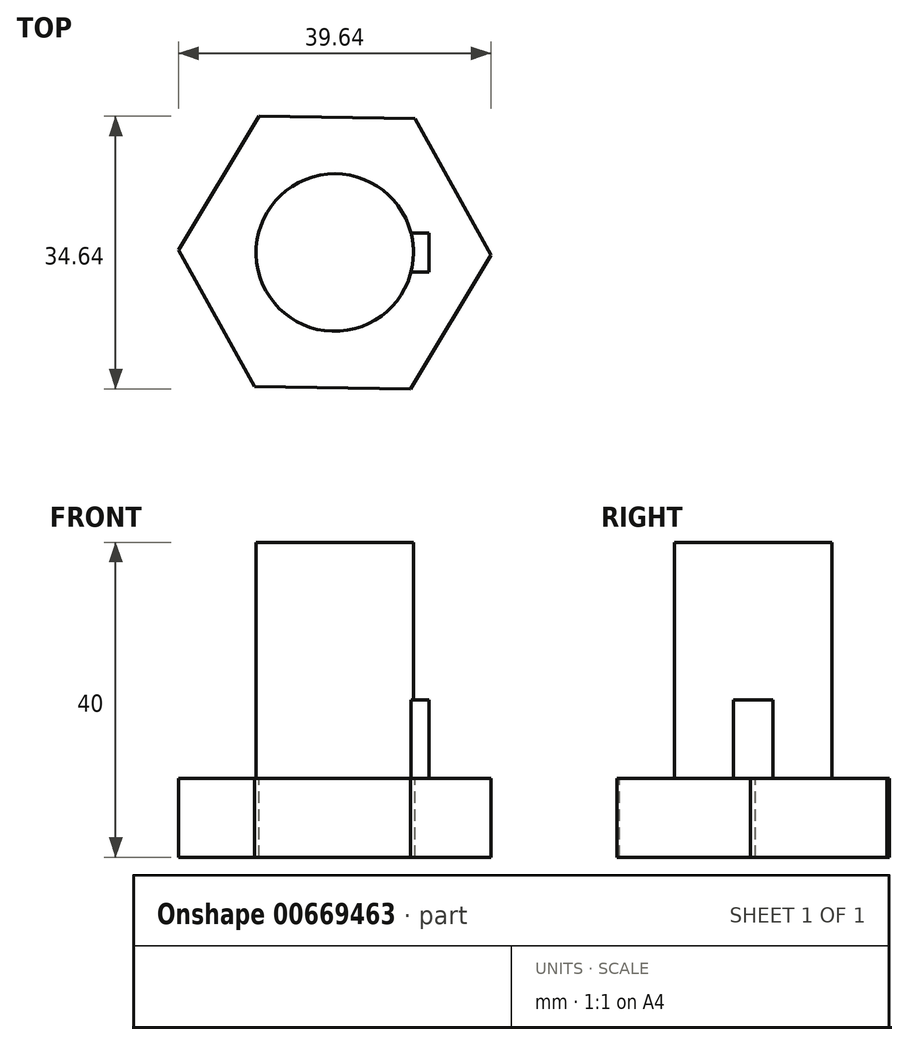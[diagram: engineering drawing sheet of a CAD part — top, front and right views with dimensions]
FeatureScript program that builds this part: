
annotation { "Feature Type Name" : "Feature", "Feature Type Description" : "" }
export const myFeature = defineFeature(function(context is Context, id is Id, definition is map)
    precondition{}
    {
        {
            var Q0;
            Q0=qCreatedBy(makeId("Top.planeOp"),FACE);
            var sketch = newSketch(context, id + "F0", { "sketchPlane" : qUnion([Q0])});
            skCircle(sketch, "E0", {"center": v(0, 0) * mm, "radius": 10 * mm});
            skLineSegment(sketch, "E1.bottom", {"start": v(9.68, 2.5) * mm, "end": v(12, 2.5) * mm});
            skLineSegment(sketch, "E1.top", {"start": v(9.68, -2.5) * mm, "end": v(12, -2.5) * mm});
            skLineSegment(sketch, "E1.right", {"start": v(12, 2.5) * mm, "end": v(12, -2.5) * mm});
            skLineSegment(sketch, "E2.0", {"start": v(-19.95, 0.1) * mm, "end": v(-9.9, 17.32) * mm});
            skLineSegment(sketch, "E2.1", {"start": v(-9.9, 17.32) * mm, "end": v(10.05, 17.23) * mm});
            skLineSegment(sketch, "E2.2", {"start": v(10.05, 17.23) * mm, "end": v(19.95, -0.1) * mm});
            skLineSegment(sketch, "E2.3", {"start": v(19.95, -0.1) * mm, "end": v(9.9, -17.32) * mm});
            skLineSegment(sketch, "E2.4", {"start": v(9.9, -17.32) * mm, "end": v(-10.05, -17.23) * mm});
            skLineSegment(sketch, "E2.5", {"start": v(-10.05, -17.23) * mm, "end": v(-19.95, 0.1) * mm});
            skSolve(sketch);
        }
        {
            var Q0;
            {var subQ0=sQuery(id+"F0.wireOp",EDGE,"E0");var subQ1=makeQuery(id+"F0.imprint","INTERSECT",VERTEX,{"derivedFrom":[subQ0,sQuery(id+"F0.wireOp",EDGE,"E1.bottom")]});Q0=makeQuery(id+"F0.imprint","IMPRINT",FACE,{"disambiguationData":[TD([[makeQuery(id+"F0.imprint","IMPRINT",EDGE,{"disambiguationData":[TD([[subQ1,-1.0]])],"derivedFrom":subQ0}),1.0]])]});}
            extrude(context, id + "F1", {"entities" : qUnion([Q0]), "depth" : 30 * mm, "offsetDistance" : 25 * mm});
        }
        {
            var Q0;
            {var subQ0=sQuery(id+"F0.wireOp",EDGE,"E1.bottom");Q0=makeQuery(id+"F0.imprint","IMPRINT",FACE,{"disambiguationData":[TD([[makeQuery(id+"F0.imprint","IMPRINT",EDGE,{"derivedFrom":subQ0}),-1.0]])]});}
            extrude(context, id + "F2", {"entities" : qUnion([Q0]), "operationType" : NewBodyOperationType.ADD, "depth" : 10 * mm, "offsetDistance" : 25 * mm});
        }
        {
            var Q0;
            Q0=qCreatedBy(makeId("Top.planeOp"),FACE);
            var sketch = newSketch(context, id + "F3", { "sketchPlane" : qUnion([Q0])});
            skLineSegment(sketch, "E3.0", {"start": v(-19.82, 0.32) * mm, "end": v(-9.63, 17.32) * mm});
            skLineSegment(sketch, "E3.1", {"start": v(-9.63, 17.32) * mm, "end": v(10.18, 17) * mm});
            skLineSegment(sketch, "E3.2", {"start": v(10.18, 17) * mm, "end": v(19.82, -0.32) * mm});
            skLineSegment(sketch, "E3.3", {"start": v(19.82, -0.32) * mm, "end": v(9.63, -17.32) * mm});
            skLineSegment(sketch, "E3.4", {"start": v(9.63, -17.32) * mm, "end": v(-10.18, -17) * mm});
            skLineSegment(sketch, "E3.5", {"start": v(-10.18, -17) * mm, "end": v(-19.82, 0.32) * mm});
            skSolve(sketch);
        }
        {
            var Q0;
            Q0=makeQuery(id+"F3.imprint","IMPRINT",FACE,{"disambiguationData":[TD([[makeQuery(id+"F3.imprint","IMPRINT",EDGE,{"derivedFrom":sQuery(id+"F3.wireOp",EDGE,"E3.0")}),-1.0]])]});
            extrude(context, id + "F4", {"entities" : qUnion([Q0]), "operationType" : NewBodyOperationType.ADD, "oppositeDirection" : true, "depth" : 10 * mm, "offsetDistance" : 25 * mm});
        }
    });
